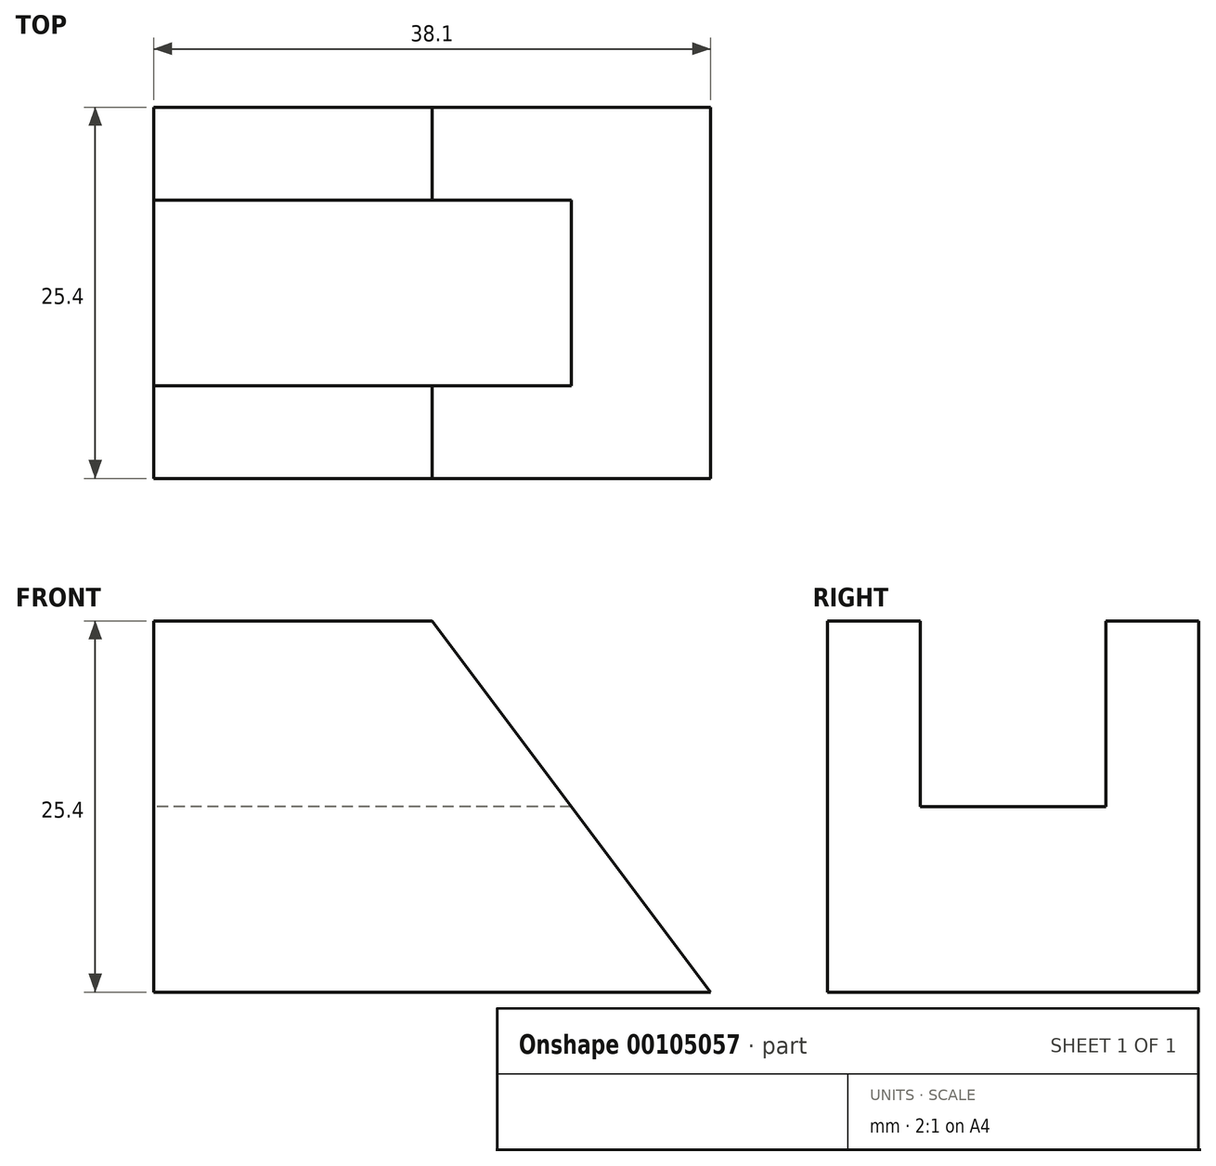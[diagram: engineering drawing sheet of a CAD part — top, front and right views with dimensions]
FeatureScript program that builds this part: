
annotation { "Feature Type Name" : "Feature", "Feature Type Description" : "" }
export const myFeature = defineFeature(function(context is Context, id is Id, definition is map)
    precondition{}
    {
        {
            var Q0;
            Q0=qCreatedBy(makeId("Right.planeOp"),FACE);
            var sketch = newSketch(context, id + "F0", { "sketchPlane" : qUnion([Q0])});
            skLineSegment(sketch, "E0.bottom", {"start": v(0, 0) * mm, "end": v(25.4, 0) * mm});
            skLineSegment(sketch, "E0.top", {"start": v(0, 25.4) * mm, "end": v(6.35, 25.4) * mm});
            skLineSegment(sketch, "E0.left", {"start": v(0, 0) * mm, "end": v(0, 25.4) * mm});
            skLineSegment(sketch, "E0.right", {"start": v(25.4, 0) * mm, "end": v(25.4, 25.4) * mm});
            skLineSegment(sketch, "E1.bottom", {"start": v(25.4, 25.4) * mm, "end": v(19.05, 25.4) * mm});
            skLineSegment(sketch, "E2.trimOffspring", {"start": v(19.05, 25.4) * mm, "end": v(25.4, 25.4) * mm});
            skLineSegment(sketch, "E3", {"start": v(6.35, 25.4) * mm, "end": v(6.35, 12.7) * mm});
            skLineSegment(sketch, "E4", {"start": v(6.35, 12.7) * mm, "end": v(19.05, 12.7) * mm});
            skLineSegment(sketch, "E5", {"start": v(19.05, 12.7) * mm, "end": v(19.05, 25.4) * mm});
            skSolve(sketch);
        }
        {
            var Q0;
            Q0=makeQuery(id+"F0.imprint","IMPRINT",FACE,{"disambiguationData":[TD([[makeQuery(id+"F0.imprint","IMPRINT",EDGE,{"derivedFrom":sQuery(id+"F0.wireOp",EDGE,"E0.bottom")}),1.0]])]});
            extrude(context, id + "F1", {"entities" : qUnion([Q0]), "depth" : 38.1 * mm});
        }
        {
            var Q0;
            Q0=qCreatedBy(makeId("Front.planeOp"),FACE);
            var sketch = newSketch(context, id + "F2", { "sketchPlane" : qUnion([Q0])});
            skLineSegment(sketch, "E6", {"start": v(19.05, 25.4) * mm, "end": v(38.1, 0) * mm});
            skLineSegment(sketch, "E7", {"start": v(38.1, 0) * mm, "end": v(38.1, 25.4) * mm});
            skLineSegment(sketch, "E8", {"start": v(38.1, 25.4) * mm, "end": v(19.05, 25.4) * mm});
            skSolve(sketch);
        }
        {
            var Q0;
            Q0 = qSketchRegion(id + "F2", true);
            extrude(context, id + "F3", {"entities" : qUnion([Q0]), "operationType" : NewBodyOperationType.REMOVE, "oppositeDirection" : true, "depth" : 25.4 * mm});
        }
    });
